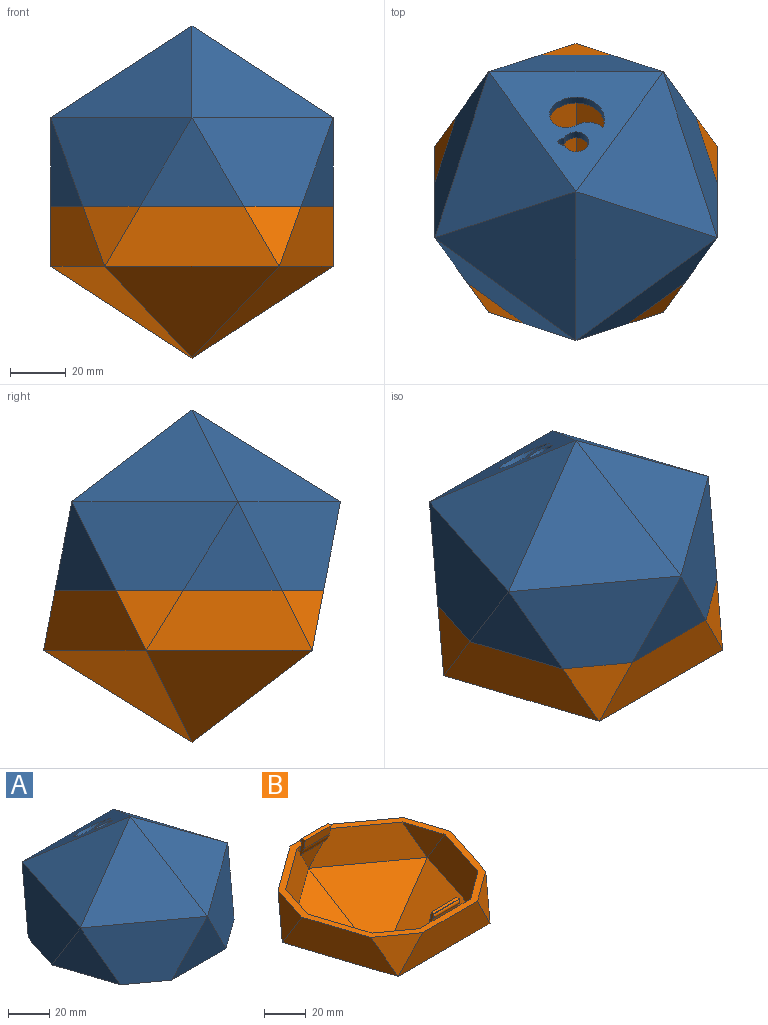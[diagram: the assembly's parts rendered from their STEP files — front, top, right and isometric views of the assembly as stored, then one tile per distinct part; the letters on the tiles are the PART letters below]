
ASSEMBLY  parts=2 mates=1
PART A: 43 faces, bbox 101.1x102.2x64.5 mm
  f0: plane 57.87x29.7mm, normal (0,-0.98,-0.19), area 1193.8mm2, adj f2,f20,f21,f26,f34,f35,f36
  f1: plane 34.91x29.7mm, normal (0,0.98,0.19), area 499.7mm2, adj f2,f24,f25,f31,f32,f33
  f2: plane 101.13x96.18mm, normal (0,0,-1), area 1072.3mm2, adj f0,f1,f3,f4,f5,f6,f7,f8
  f3: plane 35.4x31.67mm, normal (-0.93,-0.3,-0.19), area 600mm2, adj f2,f4,f12
  f4: plane 59.44x31.67mm, normal (-0.93,0.3,0.19), area 1414.8mm2, adj f2,f3,f5,f14
  f5: plane 31.67x30.12mm, normal (-0.58,0.79,-0.19), area 600mm2, adj f2,f4,f6
  f6: plane 62.5x31.67mm, normal (0,0.98,0.19), area 1414.8mm2, adj f2,f5,f7,f13
  f7: plane 31.67x30.12mm, normal (0.58,0.79,-0.19), area 600mm2, adj f2,f6,f8
  f8: plane 59.44x31.67mm, normal (0.93,0.3,0.19), area 1414.8mm2, adj f2,f7,f9,f15
  f9: plane 35.4x31.67mm, normal (0.93,-0.3,-0.19), area 600mm2, adj f2,f8,f10
  f10: plane 50.56x36.74mm, normal (0.58,-0.79,0.19), area 1414.8mm2, adj f2,f9,f11,f16
  f11: plane 37.23x31.67mm, normal (0,-0.98,-0.19), area 600mm2, adj f2,f10,f12
  f12: plane 50.56x36.74mm, normal (-0.58,-0.79,0.19), area 1414.8mm2, adj f2,f3,f11,f17
  f13: plane 62.5x43.01mm, normal (0,0.61,0.79), area 1417.1mm2, adj f6,f14,f15,f37,f38,f39,f40,f41
  f14: plane 59.44x50.56mm, normal (-0.58,0.19,0.79), area 1691.5mm2, adj f4,f13,f17
  f15: plane 59.44x50.56mm, normal (0.58,0.19,0.79), area 1691.5mm2, adj f8,f13,f16
  f16: plane 53.17x50.56mm, normal (0.36,-0.49,0.79), area 1691.5mm2, adj f10,f15,f17
  f17: plane 53.17x50.56mm, normal (-0.36,-0.49,0.79), area 1691.5mm2, adj f12,f14,f16
  f18: plane 33.2x29.7mm, normal (0.93,0.3,0.19), area 527.7mm2, adj f2,f19,f25
  f19: plane 55.04x29.7mm, normal (0.93,-0.3,-0.19), area 1221.8mm2, adj f2,f18,f20,f27
  f20: plane 29.7x28.24mm, normal (0.58,-0.79,0.19), area 527.7mm2, adj f0,f2,f19
  f21: plane 29.7x28.24mm, normal (-0.58,-0.79,0.19), area 527.7mm2, adj f0,f2,f22
  f22: plane 55.04x29.7mm, normal (-0.93,-0.3,-0.19), area 1221.8mm2, adj f2,f21,f23,f28
  f23: plane 33.2x29.7mm, normal (-0.93,0.3,0.19), area 527.7mm2, adj f2,f22,f24
  f24: plane 46.82x34.01mm, normal (-0.58,0.79,-0.19), area 1221.8mm2, adj f1,f2,f23,f29
  f25: plane 46.82x34.01mm, normal (0.58,0.79,-0.19), area 1221.8mm2, adj f1,f2,f18,f30
  f26: plane 57.87x39.83mm, normal (0,-0.61,-0.79), area 1175.7mm2, adj f0,f27,f28,f37,f38,f39,f40,f41
  f27: plane 55.04x46.82mm, normal (0.58,-0.19,-0.79), area 1450.1mm2, adj f19,f26,f30
  f28: plane 55.04x46.82mm, normal (-0.58,-0.19,-0.79), area 1450.1mm2, adj f22,f26,f29
  f29: plane 49.23x46.82mm, normal (-0.36,0.49,-0.79), area 1450.1mm2, adj f24,f28,f30
  f30: plane 49.23x46.82mm, normal (0.36,0.49,-0.79), area 1450.1mm2, adj f25,f27,f29
  f31: cylinder r=1mm len=17.5mm, axis (1,0,0), area 32.5mm2, adj f1,f32,f33
  f32: plane 1.57x0.56mm, normal (1,0,0), area 0.4mm2, adj f1,f31
  f33: plane 1.57x0.56mm, normal (-1,0,0), area 0.4mm2, adj f1,f31
  f34: cylinder r=1mm len=17.5mm, axis (1,0,0), area 32.5mm2, adj f0,f35,f36
  f35: plane 1.57x0.56mm, normal (1,0,0), area 0.4mm2, adj f0,f34
  f36: plane 1.57x0.56mm, normal (-1,0,0), area 0.4mm2, adj f0,f34
  f37: cylinder r=3.3mm len=3.84mm, axis (0,0.61,0.79), area 10.9mm2, adj f13,f26,f38,f39
  f38: cylinder r=4.5mm len=9.28mm, axis (0,0.61,0.79), area 86.4mm2, adj f13,f26,f37,f39
  f39: cylinder r=3.3mm len=3.84mm, axis (0,0.61,0.79), area 10.9mm2, adj f13,f26,f37,f38
  f40: cylinder r=10.23mm len=18.69mm, axis (0,0.61,0.79), area 103.6mm2, adj f13,f26,f41,f42
  f41: cylinder r=6mm len=9.57mm, axis (0,0.61,0.79), area 58.6mm2, adj f13,f26,f40,f42
  f42: cylinder r=7.27mm len=9.61mm, axis (0,0.61,0.79), area 37mm2, adj f13,f26,f40,f41
PART B: 49 faces, bbox 101.1x100.3x59.6 mm
  f0: plane 17.5x0.44mm, normal (0,-0.98,-0.19), area 7.9mm2, adj f42,f43,f44,f47
  f1: plane 17.5x0.44mm, normal (0,0.98,0.19), area 7.9mm2, adj f35,f36,f37,f40
  f2: plane 46.83x34.03mm, normal (0.58,-0.79,0.19), area 921.6mm2, adj f3,f4,f6,f23,f34,f36,f41
  f3: plane 15.45x13.15mm, normal (0,-0.98,-0.19), area 103.4mm2, adj f2,f5,f41
  f4: plane 4.64x2.73mm, normal (0,-0.98,-0.19), area 6.5mm2, adj f2,f6,f36
  f5: plane 46.83x34.03mm, normal (-0.58,-0.79,0.19), area 921.6mm2, adj f3,f6,f24,f25,f31,f37,f41
  f6: plane 101.13x96.18mm, normal (0,0,1), area 1072.3mm2, adj f2,f4,f5,f7,f8,f9,f10,f11
  f7: plane 59.44x21.5mm, normal (-0.93,-0.3,-0.19), area 1091.4mm2, adj f6,f8,f16,f20
  f8: plane 24.04x21.5mm, normal (-0.93,0.3,0.19), area 276.6mm2, adj f6,f7,f9
  f9: plane 50.56x36.74mm, normal (-0.58,0.79,-0.19), area 1091.4mm2, adj f6,f8,f10,f21
  f10: plane 25.27x21.5mm, normal (0,0.98,0.19), area 276.6mm2, adj f6,f9,f11
  f11: plane 50.56x36.74mm, normal (0.58,0.79,-0.19), area 1091.4mm2, adj f6,f10,f12,f18
  f12: plane 24.04x21.5mm, normal (0.93,0.3,0.19), area 276.6mm2, adj f6,f11,f13
  f13: plane 59.44x21.5mm, normal (0.93,-0.3,-0.19), area 1091.4mm2, adj f6,f12,f14,f17
  f14: plane 21.5x20.45mm, normal (0.58,-0.79,0.19), area 276.6mm2, adj f6,f13,f15
  f15: plane 62.5x21.5mm, normal (0,-0.98,-0.19), area 1091.4mm2, adj f6,f14,f16,f19
  f16: plane 21.5x20.45mm, normal (-0.58,-0.79,0.19), area 276.6mm2, adj f6,f7,f15
  f17: plane 59.44x50.56mm, normal (0.58,-0.19,-0.79), area 1691.5mm2, adj f13,f18,f19
  f18: plane 53.17x50.56mm, normal (0.36,0.49,-0.79), area 1691.5mm2, adj f11,f17,f21
  f19: plane 62.5x43.01mm, normal (0,-0.61,-0.79), area 1691.5mm2, adj f15,f17,f20
  f20: plane 59.44x50.56mm, normal (-0.58,-0.19,-0.79), area 1691.5mm2, adj f7,f19,f21
  f21: plane 53.17x50.56mm, normal (-0.36,0.49,-0.79), area 1691.5mm2, adj f9,f18,f20
  f22: plane 55.04x19.53mm, normal (0.93,0.3,0.19), area 922.4mm2, adj f6,f23,f29,f33
  f23: plane 21.84x19.53mm, normal (0.93,-0.3,-0.19), area 228.3mm2, adj f2,f6,f22
  f24: plane 4.64x2.73mm, normal (0,-0.98,-0.19), area 6.5mm2, adj f5,f6,f37
  f25: plane 21.84x19.53mm, normal (-0.93,-0.3,-0.19), area 228.3mm2, adj f5,f6,f26
  f26: plane 55.04x19.53mm, normal (-0.93,0.3,0.19), area 922.4mm2, adj f6,f25,f27,f30
  f27: plane 19.53x18.57mm, normal (-0.58,0.79,-0.19), area 228.3mm2, adj f6,f26,f28
  f28: plane 57.87x19.53mm, normal (0,0.98,0.19), area 808.6mm2, adj f6,f27,f29,f32,f43,f44,f48
  f29: plane 19.53x18.57mm, normal (0.58,0.79,-0.19), area 228.3mm2, adj f6,f22,f28
  f30: plane 55.04x46.82mm, normal (-0.58,0.19,0.79), area 1450.1mm2, adj f26,f31,f32
  f31: plane 49.23x46.82mm, normal (-0.36,-0.49,0.79), area 1450.1mm2, adj f5,f30,f34
  f32: plane 57.87x39.83mm, normal (0,0.61,0.79), area 1450.1mm2, adj f28,f30,f33
  f33: plane 55.04x46.82mm, normal (0.58,0.19,0.79), area 1450.1mm2, adj f22,f32,f34
  f34: plane 49.23x46.82mm, normal (0.36,-0.49,0.79), area 1450.1mm2, adj f2,f31,f33
  f35: plane 17.5x1.96mm, normal (0,-0.19,0.98), area 35mm2, adj f1,f36,f37,f38
  f36: plane 10.7x3.79mm, normal (-1,0,0), area 20.1mm2, adj f1,f2,f4,f35,f38,f39,f40,f41
  f37: plane 10.7x3.79mm, normal (1,0,0), area 20.1mm2, adj f1,f5,f24,f35,f38,f39,f40,f41
  f38: plane 17.5x5.4mm, normal (0,-0.98,-0.19), area 96.2mm2, adj f35,f36,f37,f41
  f39: plane 17.5x1.92mm, normal (0,0.98,0.19), area 34.1mm2, adj f6,f36,f37,f40
  f40: cylinder r=1.5mm len=17.5mm, axis (1,0,0), area 55mm2, adj f1,f36,f37,f39
  f41: cylinder r=10mm len=17.5mm, axis (-1,0,0), area 111.7mm2, adj f2,f3,f5,f36,f37,f38
  f42: plane 17.5x1.47mm, normal (0,-0.19,0.98), area 26.2mm2, adj f0,f43,f44,f45
  f43: plane 11.58x3.35mm, normal (1,0,0), area 16.5mm2, adj f0,f28,f42,f45,f46,f47,f48
  f44: plane 11.58x3.35mm, normal (-1,0,0), area 16.5mm2, adj f0,f28,f42,f45,f46,f47,f48
  f45: plane 17.5x6.88mm, normal (0,0.98,0.19), area 122.5mm2, adj f42,f43,f44,f48
  f46: plane 17.5x1.92mm, normal (0,-0.98,-0.19), area 34.1mm2, adj f6,f43,f44,f47
  f47: cylinder r=1.5mm len=17.5mm, axis (-1,0,0), area 55mm2, adj f0,f43,f44,f46
  f48: cylinder r=7.5mm len=17.5mm, axis (1,0,0), area 84.5mm2, adj f28,f43,f44,f45
PLACE A t=(5.82,-18.84,-29.75)mm
PLACE B t=(5.82,-18.84,-29.75)mm
MATE fastened A.f2 <-> B.f6  axis (0,0,-1) through (5.82,-18.84,-8.25)mm
